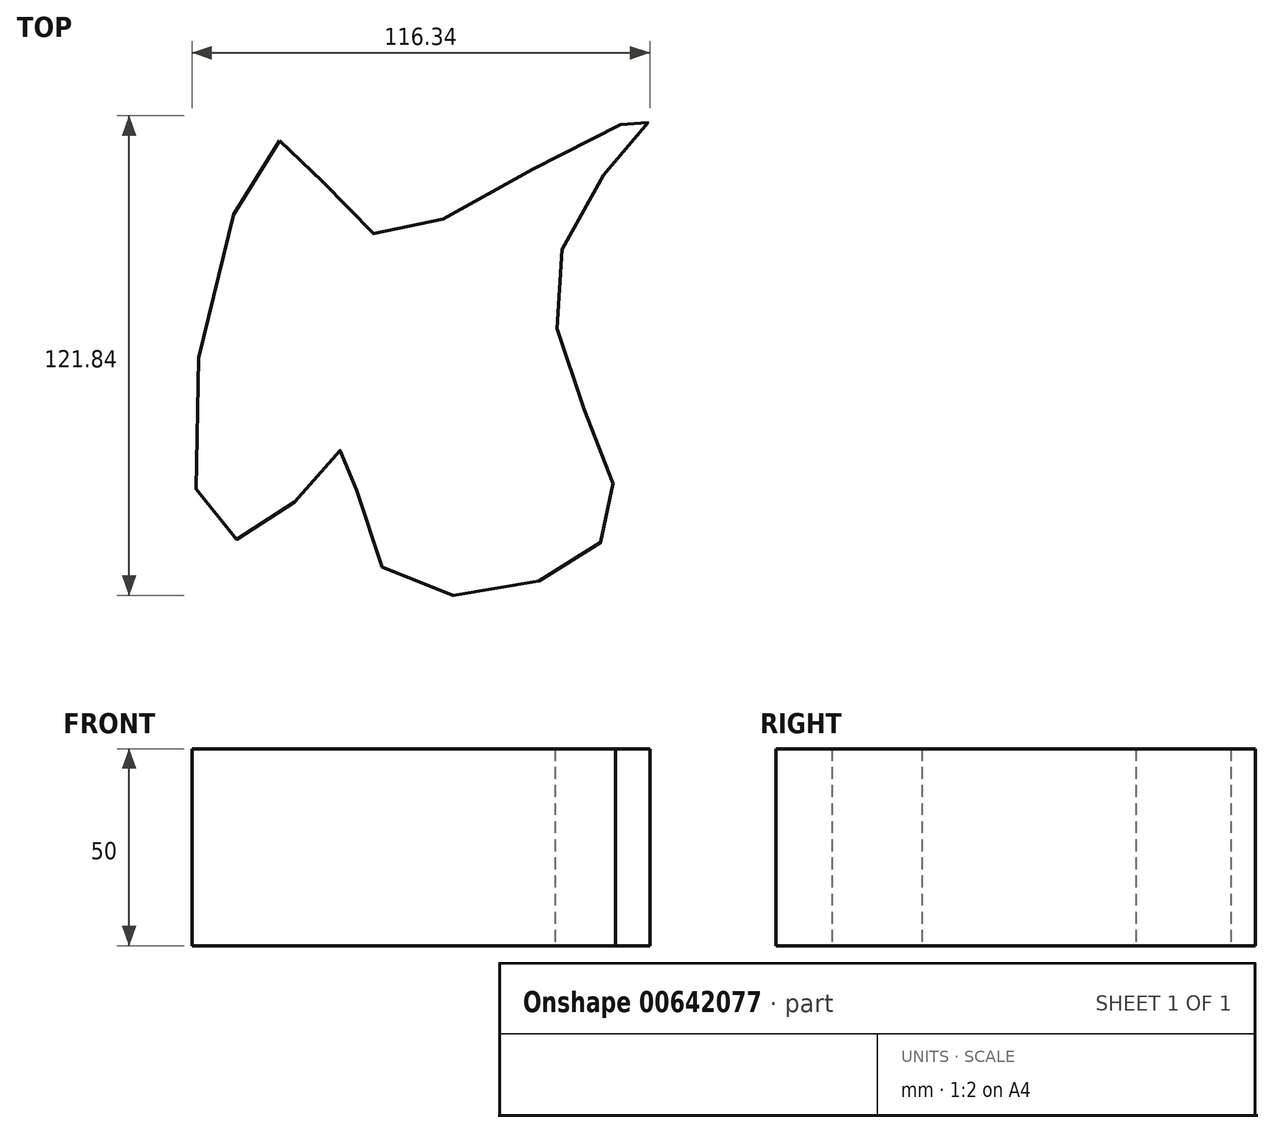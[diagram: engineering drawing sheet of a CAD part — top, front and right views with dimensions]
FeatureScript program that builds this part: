
annotation { "Feature Type Name" : "Feature", "Feature Type Description" : "" }
export const myFeature = defineFeature(function(context is Context, id is Id, definition is map)
    precondition{}
    {
        {
            var Q0;
            Q0=qCreatedBy(makeId("Top.planeOp"),FACE);
            var sketch = newSketch(context, id + "F0", { "sketchPlane" : qUnion([Q0])});
            skFitSpline(sketch, "E0", {"points": [v(-39.68, 56.08) * mm, v(-60.68, -33.57) * mm, v(-44.08, -43.34) * mm, v(-23.08, -22.34) * mm, v(-14.77, -50.67) * mm, v(23.8, -56.54) * mm, v(45.54, -37.97) * mm, v(32.84, 0) * mm, v(37.48, 40.2) * mm, v(54.33, 62.19) * mm, v(16.48, 44.35) * mm, v(-19.9, 34.58) * mm, v(-39.68, 56.08) * mm]});
            skSolve(sketch);
        }
        {
            var Q0;
            Q0=makeQuery(id+"F0.imprint","IMPRINT",FACE,{"disambiguationData":[TD([[makeQuery(id+"F0.imprint","IMPRINT",EDGE,{"derivedFrom":sQuery(id+"F0.wireOp",EDGE,"E0")}),1.0]])]});
            extrude(context, id + "F1", {"entities" : qUnion([Q0]), "depth" : 50 * mm, "offsetDistance" : 25.4 * mm});
        }
    });
